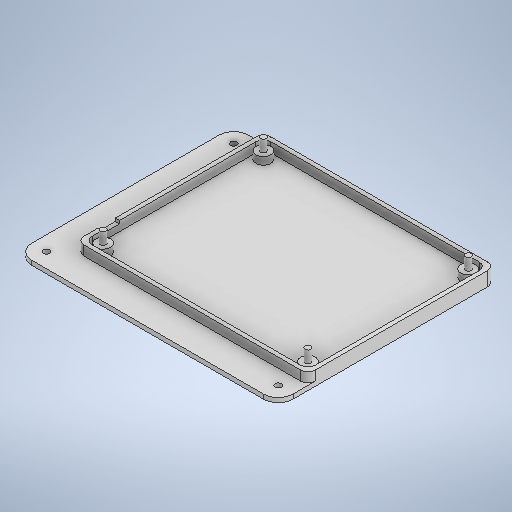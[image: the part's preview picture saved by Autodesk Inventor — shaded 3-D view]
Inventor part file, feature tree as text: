
AUTODESK INVENTOR PART (.ipt)
format: ipt  version: 2025.2 (Build 292293000, 293)  size: 361,984 bytes
history: native  units: mm
features: extrude x6, sketch x4, fillet x3
ambient origin geometry x8: Origin, YZ Plane, XZ Plane, XY Plane, X Axis, Y Axis, Z Axis, Center Point
bodies: Solid1 (feature_tree)
feature tree (13):
  sketch  "Sketch1"  dims[d4=176.0mm d5=146.0mm]
  extrude  "Extrusion1"  Depth=146.0mm
  extrude  "Extrusion2"  Depth=20.0mm
  extrude  "Extrusion4"  Depth=3.0mm
  fillet  "Fillet1"  Radius=3.0mm
  extrude  "Extrusion5"  Depth=2.8mm
  fillet  "Fillet2"  Radius=2.8mm
  fillet  "Fillet3"  Radius=2.8mm
  extrude  "Extrusion6"  Depth=2.8mm
  extrude  "Extrusion7"  Depth=2.0mm
  sketch  "Sketch2"  dims[d6=20.0mm d7=20.0mm]
  sketch  "Sketch3"  dims[d8=3.0mm d9=3.0mm d10=3.0mm]
  sketch  "Sketch4"  dims[d11=3.0mm d12=2.8mm d13=2.8mm d14=2.8mm d15=2.8mm d16=6.0mm d17=6.0mm d18=6.0mm d19=6.0mm d20=6.0mm d21=6.0mm d22=6.0mm d23=6.0mm d24=10.0mm d25=10.0mm d26=10.0mm d27=10.0mm d28=5.0mm d29=5.0mm d30=5.0mm d31=5.0mm d32=5.0mm d33=5.0mm d34=5.0mm d35=5.0mm d36=3.0mm d37=0.0mm d38=5.0mm d39=0.0mm d42=6.5mm d43=0.0mm d44=5.0mm d45=3.9mm d46=3.9mm d47=3.9mm d48=3.9mm d49=8.0mm d50=0.0mm d51=5.0mm d52=10.0mm d53=20.0mm d54=20.0mm d55=20.0mm d56=20.0mm d57=4.3mm d58=4.3mm d59=4.3mm d60=8.0mm d61=0.0mm d62=14.25mm d63=12.0mm d64=2.0mm d65=0.0mm]
